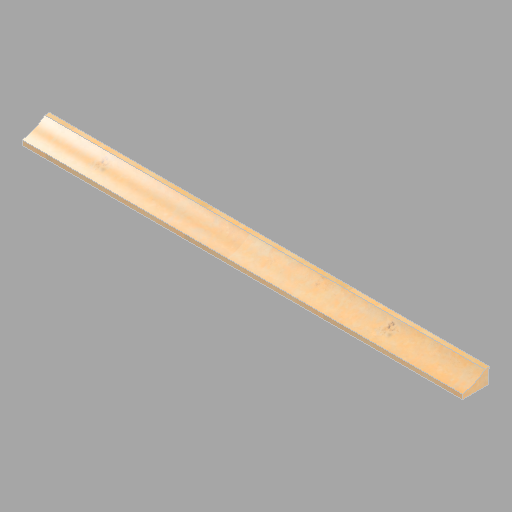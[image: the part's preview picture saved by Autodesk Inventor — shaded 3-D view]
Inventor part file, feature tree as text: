
AUTODESK INVENTOR PART (.ipt)
format: ipt  version: 2022.2 (Build 262287010, 287A)  size: 165,888 bytes
history: native  units: in
note: dims shown in document units (in); Inventor stores cm internally (conversion verified against a paired STEP export)
features: revolve x2, other x1, direct_edit x1
ambient origin geometry x8: Origin, YZ Plane, XZ Plane, XY Plane, X Axis, Y Axis, Z Axis, Center Point
bodies: Solid1 (feature_tree)
feature tree (4):
  other  "North (3)"
  direct_edit  "Direct Edit1"
  revolve  "Rotate1"  [1 undecoded]
  revolve  "Rotate2"  Angle=90.0deg
note: 1 required parameter value undecoded (feature->parameter linkage not recoverable at this tier; creation-order binding heuristic only, values carry confidence <= 0.55)
